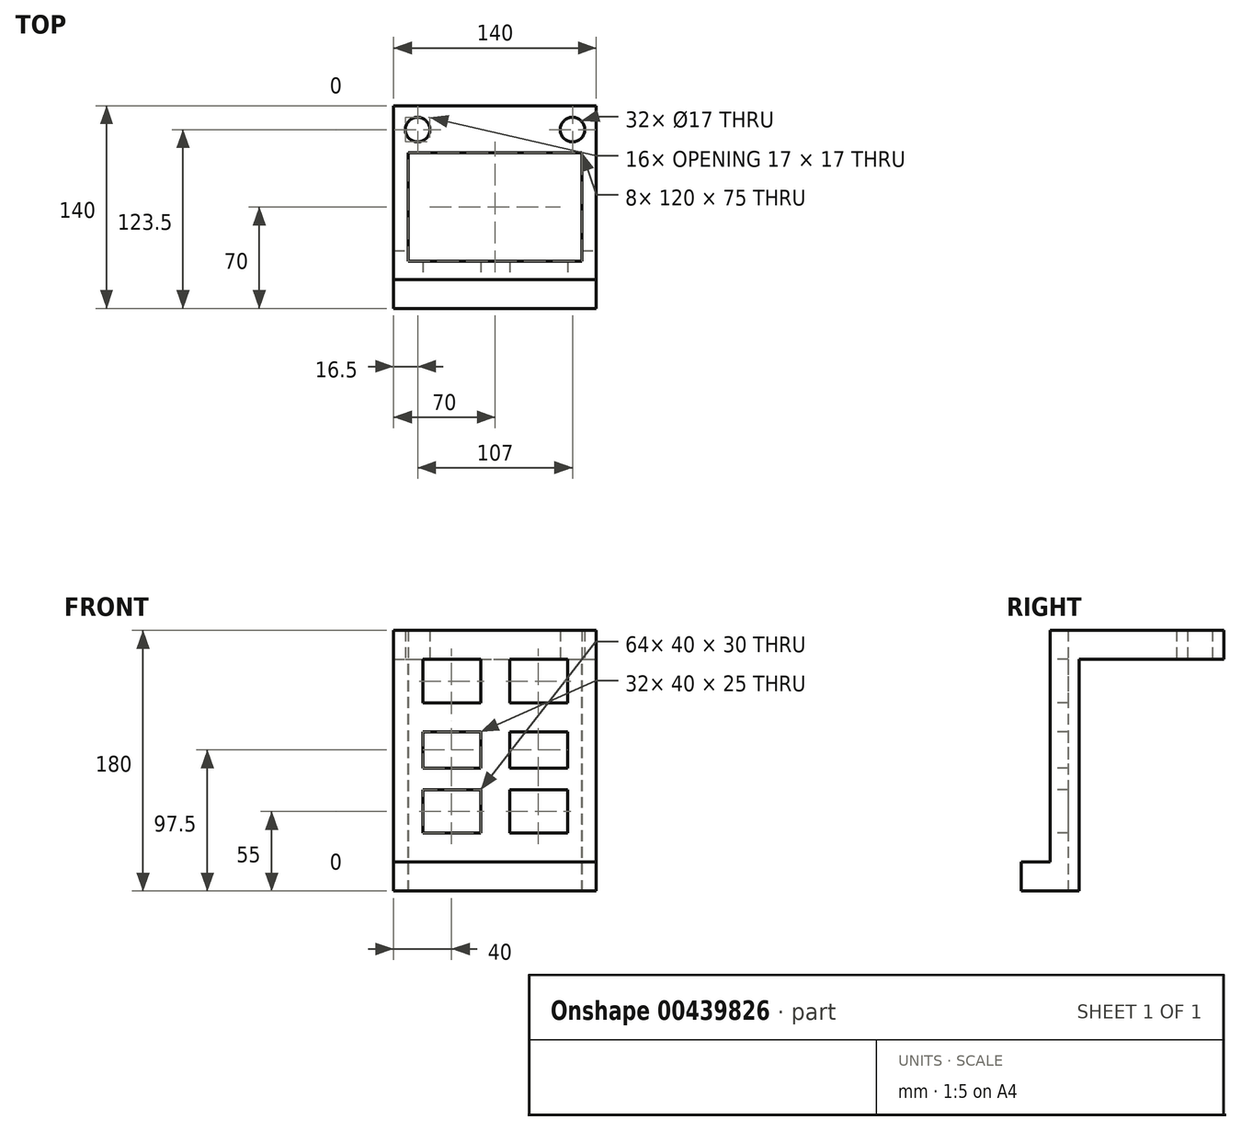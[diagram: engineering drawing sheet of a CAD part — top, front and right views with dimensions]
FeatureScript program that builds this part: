
annotation { "Feature Type Name" : "Feature", "Feature Type Description" : "" }
export const myFeature = defineFeature(function(context is Context, id is Id, definition is map)
    precondition{}
    {
        {
            var Q0;
            Q0=qCreatedBy(makeId("Top.planeOp"),FACE);
            var sketch = newSketch(context, id + "F0", { "sketchPlane" : qUnion([Q0])});
            skLineSegment(sketch, "E0.bottom", {"start": v(70, 70) * mm, "end": v(-70, 70) * mm});
            skLineSegment(sketch, "E0.top", {"start": v(70, -70) * mm, "end": v(-70, -70) * mm});
            skLineSegment(sketch, "E0.left", {"start": v(70, 70) * mm, "end": v(70, -70) * mm});
            skLineSegment(sketch, "E0.right", {"start": v(-70, 70) * mm, "end": v(-70, -70) * mm});
            skPoint(sketch, "E0.middle", {"position": v(0, 0) * mm});
            skCircle(sketch, "E1", {"center": v(-53.5, 53.5) * mm, "radius": 8.5 * mm});
            skCircle(sketch, "E2", {"center": v(53.5, 53.5) * mm, "radius": 8.5 * mm});
            skLineSegment(sketch, "E3.bottom", {"start": v(60, -37.5) * mm, "end": v(-60, -37.5) * mm});
            skLineSegment(sketch, "E3.top", {"start": v(60, 37.5) * mm, "end": v(-60, 37.5) * mm});
            skLineSegment(sketch, "E3.left", {"start": v(60, -37.5) * mm, "end": v(60, 37.5) * mm});
            skLineSegment(sketch, "E3.right", {"start": v(-60, -37.5) * mm, "end": v(-60, 37.5) * mm});
            skSolve(sketch);
        }
        {
            var Q0;
            Q0 = qSketchRegion(id + "F0", true);
            var Q1;
            Q1 = qSketchRegion(id + "F2", true);
            var Q2;
            Q2 = qSketchRegion(id + "F4", true);
            extrude(context, id + "F1", {"entities" : qUnion([Q0, Q1, Q2]), "depth" : 180 * mm});
        }
        {
            var Q0;
            Q0=makeQuery(id+"F1.opExtrude","SWEPT_FACE",FACE,{"disambiguationData":[OSD([sQuery(id+"F0.wireOp",EDGE,"E0.left")])]});
            var sketch = newSketch(context, id + "F2", { "sketchPlane" : qUnion([Q0])});
            skPoint(sketch, "E4", {"position": v(-50, 180) * mm});
            skPoint(sketch, "E5", {"position": v(-50, 20) * mm});
            skPoint(sketch, "E6", {"position": v(-30, 160) * mm});
            skLineSegment(sketch, "E7", {"start": v(-50, 180) * mm, "end": v(-50, 20) * mm});
            skLineSegment(sketch, "E8", {"start": v(-50, 20) * mm, "end": v(-70, 20) * mm});
            skLineSegment(sketch, "E9", {"start": v(-30, 160) * mm, "end": v(-30, 0) * mm});
            skLineSegment(sketch, "E10", {"start": v(-30, 160) * mm, "end": v(70, 160) * mm});
            skSolve(sketch);
        }
        {
            var Q0;
            {var subQ0=sQuery(id+"F2.wireOp",EDGE,"E7");Q0=makeQuery(id+"F2.imprint","IMPRINT",FACE,{"disambiguationData":[TD([[makeQuery(id+"F2.imprint","IMPRINT",EDGE,{"derivedFrom":subQ0}),-1.0]])]});}
            var Q1;
            {var subQ0=sQuery(id+"F2.wireOp",EDGE,"E9");Q1=makeQuery(id+"F2.imprint","IMPRINT",FACE,{"disambiguationData":[TD([[makeQuery(id+"F2.imprint","IMPRINT",EDGE,{"derivedFrom":subQ0}),1.0]])]});}
            extrude(context, id + "F3", {"entities" : qUnion([Q0, Q1]), "operationType" : NewBodyOperationType.REMOVE, "oppositeDirection" : true, "depth" : 140 * mm});
        }
        {
            var Q0;
            Q0=makeQuery(id+"F3.boolean.opBoolean","COPY",FACE,{"derivedFrom":makeQuery(id+"F3.opExtrude","SWEPT_FACE",FACE,{"disambiguationData":[OSD([sQuery(id+"F2.wireOp",EDGE,"E7")])]})});
            var sketch = newSketch(context, id + "F4", { "sketchPlane" : qUnion([Q0])});
            skLineSegment(sketch, "E11.bottom", {"start": v(-50, 160) * mm, "end": v(-10, 160) * mm});
            skLineSegment(sketch, "E11.top", {"start": v(-50, 130) * mm, "end": v(-10, 130) * mm});
            skLineSegment(sketch, "E11.left", {"start": v(-50, 160) * mm, "end": v(-50, 130) * mm});
            skLineSegment(sketch, "E11.right", {"start": v(-10, 160) * mm, "end": v(-10, 130) * mm});
            skLineSegment(sketch, "E12.bottom", {"start": v(-50, 70) * mm, "end": v(-10, 70) * mm});
            skLineSegment(sketch, "E12.top", {"start": v(-50, 40) * mm, "end": v(-10, 40) * mm});
            skLineSegment(sketch, "E12.left", {"start": v(-50, 70) * mm, "end": v(-50, 40) * mm});
            skLineSegment(sketch, "E12.right", {"start": v(-10, 70) * mm, "end": v(-10, 40) * mm});
            skLineSegment(sketch, "E13.bottom", {"start": v(10, 160) * mm, "end": v(50, 160) * mm});
            skLineSegment(sketch, "E13.top", {"start": v(10, 130) * mm, "end": v(50, 130) * mm});
            skLineSegment(sketch, "E13.left", {"start": v(10, 160) * mm, "end": v(10, 130) * mm});
            skLineSegment(sketch, "E13.right", {"start": v(50, 160) * mm, "end": v(50, 130) * mm});
            skLineSegment(sketch, "E14.bottom", {"start": v(10, 70) * mm, "end": v(50, 70) * mm});
            skLineSegment(sketch, "E14.top", {"start": v(10, 40) * mm, "end": v(50, 40) * mm});
            skLineSegment(sketch, "E14.left", {"start": v(10, 70) * mm, "end": v(10, 40) * mm});
            skLineSegment(sketch, "E14.right", {"start": v(50, 70) * mm, "end": v(50, 40) * mm});
            skLineSegment(sketch, "E15.bottom", {"start": v(-50, 110) * mm, "end": v(-10, 110) * mm});
            skLineSegment(sketch, "E15.top", {"start": v(-50, 85) * mm, "end": v(-10, 85) * mm});
            skLineSegment(sketch, "E15.left", {"start": v(-50, 110) * mm, "end": v(-50, 85) * mm});
            skLineSegment(sketch, "E15.right", {"start": v(-10, 110) * mm, "end": v(-10, 85) * mm});
            skLineSegment(sketch, "E16.bottom", {"start": v(10, 110) * mm, "end": v(50, 110) * mm});
            skLineSegment(sketch, "E16.top", {"start": v(10, 85) * mm, "end": v(50, 85) * mm});
            skLineSegment(sketch, "E16.left", {"start": v(10, 110) * mm, "end": v(10, 85) * mm});
            skLineSegment(sketch, "E16.right", {"start": v(50, 110) * mm, "end": v(50, 85) * mm});
            skSolve(sketch);
        }
        {
            var Q0;
            Q0=makeQuery(id+"F4.imprint","IMPRINT",FACE,{"disambiguationData":[TD([[makeQuery(id+"F4.imprint","IMPRINT",EDGE,{"derivedFrom":sQuery(id+"F4.wireOp",EDGE,"E11.bottom")}),-1.0]])]});
            var Q1;
            Q1=makeQuery(id+"F4.imprint","IMPRINT",FACE,{"disambiguationData":[TD([[makeQuery(id+"F4.imprint","IMPRINT",EDGE,{"derivedFrom":sQuery(id+"F4.wireOp",EDGE,"E13.bottom")}),-1.0]])]});
            var Q2;
            Q2=makeQuery(id+"F4.imprint","IMPRINT",FACE,{"disambiguationData":[TD([[makeQuery(id+"F4.imprint","IMPRINT",EDGE,{"derivedFrom":sQuery(id+"F4.wireOp",EDGE,"E14.bottom")}),-1.0]])]});
            var Q3;
            Q3=makeQuery(id+"F4.imprint","IMPRINT",FACE,{"disambiguationData":[TD([[makeQuery(id+"F4.imprint","IMPRINT",EDGE,{"derivedFrom":sQuery(id+"F4.wireOp",EDGE,"E12.bottom")}),-1.0]])]});
            var Q4;
            Q4=makeQuery(id+"F4.imprint","IMPRINT",FACE,{"disambiguationData":[TD([[makeQuery(id+"F4.imprint","IMPRINT",EDGE,{"derivedFrom":sQuery(id+"F4.wireOp",EDGE,"E15.bottom")}),-1.0]])]});
            var Q5;
            Q5=makeQuery(id+"F4.imprint","IMPRINT",FACE,{"disambiguationData":[TD([[makeQuery(id+"F4.imprint","IMPRINT",EDGE,{"derivedFrom":sQuery(id+"F4.wireOp",EDGE,"E16.bottom")}),-1.0]])]});
            extrude(context, id + "F5", {"entities" : qUnion([Q0, Q1, Q2, Q3, Q4, Q5]), "operationType" : NewBodyOperationType.REMOVE, "oppositeDirection" : true, "depth" : 20 * mm, "offsetDistance" : 25 * mm});
        }
    });
